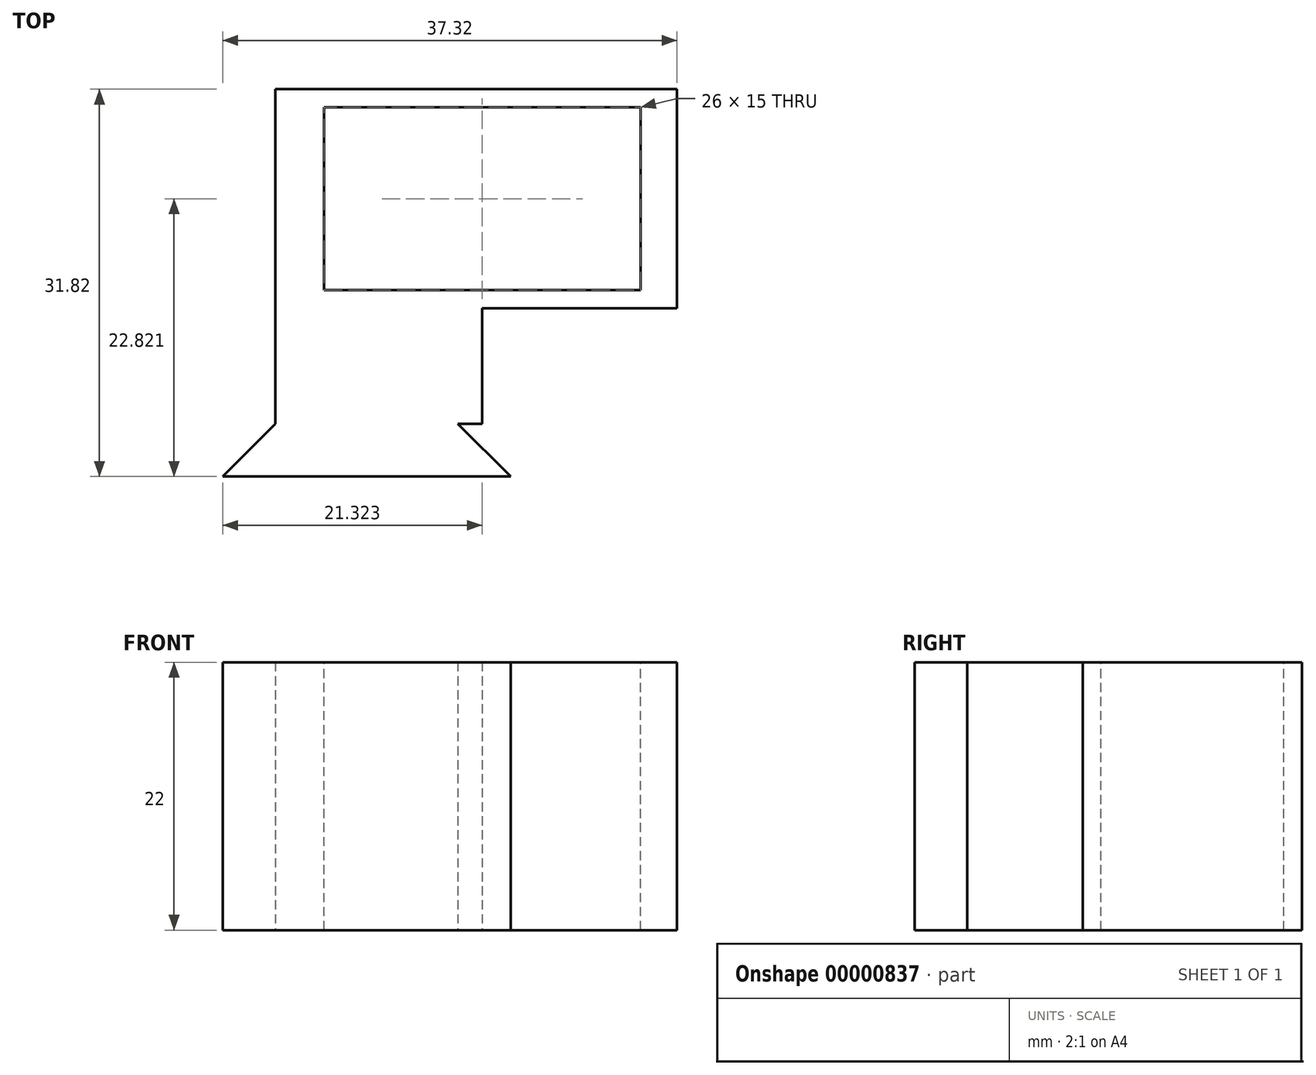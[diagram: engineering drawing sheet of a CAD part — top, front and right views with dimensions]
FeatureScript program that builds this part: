
annotation { "Feature Type Name" : "Feature", "Feature Type Description" : "" }
export const myFeature = defineFeature(function(context is Context, id is Id, definition is map)
    precondition{}
    {
        {
            var Q0;
            Q0=qCreatedBy(makeId("Top.planeOp"),FACE);
            var sketch = newSketch(context, id + "F0", { "sketchPlane" : qUnion([Q0])});
            skLineSegment(sketch, "E0", {"start": v(-62.25, 112.26) * mm, "end": v(-66.58, 116.58) * mm});
            skLineSegment(sketch, "E1", {"start": v(-74.08, 165.58) * mm, "end": v(-74.08, 36.8) * mm, "construction": true});
            skLineSegment(sketch, "E2.0.MirrorCS", {"start": v(-81.58, 116.58) * mm, "end": v(-81.58, 126.08) * mm});
            skLineSegment(sketch, "E3.0.MirrorCS", {"start": v(-85.9, 112.26) * mm, "end": v(-81.58, 116.58) * mm});
            skLineSegment(sketch, "E4.top", {"start": v(-66.58, 116.58) * mm, "end": v(-64.58, 116.58) * mm});
            skLineSegment(sketch, "E4.right", {"start": v(-64.58, 126.08) * mm, "end": v(-64.58, 116.58) * mm});
            skLineSegment(sketch, "E5", {"start": v(-81.58, 126.08) * mm, "end": v(-81.58, 144.08) * mm});
            skLineSegment(sketch, "E6", {"start": v(-81.58, 144.08) * mm, "end": v(-48.58, 144.08) * mm});
            skLineSegment(sketch, "E7", {"start": v(-64.58, 126.08) * mm, "end": v(-48.58, 126.08) * mm});
            skLineSegment(sketch, "E8", {"start": v(-48.58, 126.08) * mm, "end": v(-48.58, 144.08) * mm});
            skPoint(sketch, "E9.end.orphan", {"position": v(-76.58, 126.08) * mm});
            skLineSegment(sketch, "E10", {"start": v(-85.9, 112.26) * mm, "end": v(-62.25, 112.26) * mm});
            skSolve(sketch);
        }
        {
            var Q0;
            Q0 = qSketchRegion(id + "F0", true);
            var Q1;
            Q1=makeQuery(id+"F0.imprint","IMPRINT",FACE,{"disambiguationData":[TD([[makeQuery(id+"F0.imprint","IMPRINT",EDGE,{"derivedFrom":sQuery(id+"F0.wireOp",EDGE,"E0")}),1.0]])]});
            extrude(context, id + "F1", {"entities" : qUnion([Q0, Q1]), "depth" : 22 * mm});
        }
        {
            var Q0;
            Q0=makeQuery(id+"F1.opExtrude","CAP_FACE",FACE,{"disambiguationData":[OSD([sQuery(id+"F0.wireOp",EDGE,"E0"),sQuery(id+"F0.wireOp",EDGE,"E3.0.MirrorCS"),sQuery(id+"F0.wireOp",EDGE,"E4.top"),sQuery(id+"F0.wireOp",EDGE,"E4.right"),sQuery(id+"F0.wireOp",EDGE,"E5"),sQuery(id+"F0.wireOp",EDGE,"E6"),sQuery(id+"F0.wireOp",EDGE,"E7"),sQuery(id+"F0.wireOp",EDGE,"E8"),sQuery(id+"F0.wireOp",EDGE,"E10")])],"isStart":false});
            var sketch = newSketch(context, id + "F2", { "sketchPlane" : qUnion([Q0])});
            skLineSegment(sketch, "E11.1", {"start": v(-51.58, 127.58) * mm, "end": v(-51.58, 142.58) * mm});
            skLineSegment(sketch, "E11.2", {"start": v(-77.58, 142.58) * mm, "end": v(-51.58, 142.58) * mm});
            skLineSegment(sketch, "E11.3", {"start": v(-77.58, 127.58) * mm, "end": v(-77.58, 142.58) * mm});
            skLineSegment(sketch, "E12", {"start": v(-51.58, 127.58) * mm, "end": v(-77.58, 127.58) * mm});
            skSolve(sketch);
        }
        {
            var Q0;
            Q0=makeQuery(id+"F2.imprint","IMPRINT",FACE,{"disambiguationData":[TD([[makeQuery(id+"F2.imprint","IMPRINT",EDGE,{"derivedFrom":sQuery(id+"F2.wireOp",EDGE,"E11.1")}),1.0]])]});
            extrude(context, id + "F3", {"entities" : qUnion([Q0]), "operationType" : NewBodyOperationType.REMOVE, "oppositeDirection" : true, "depth" : 29 * mm});
        }
    });
